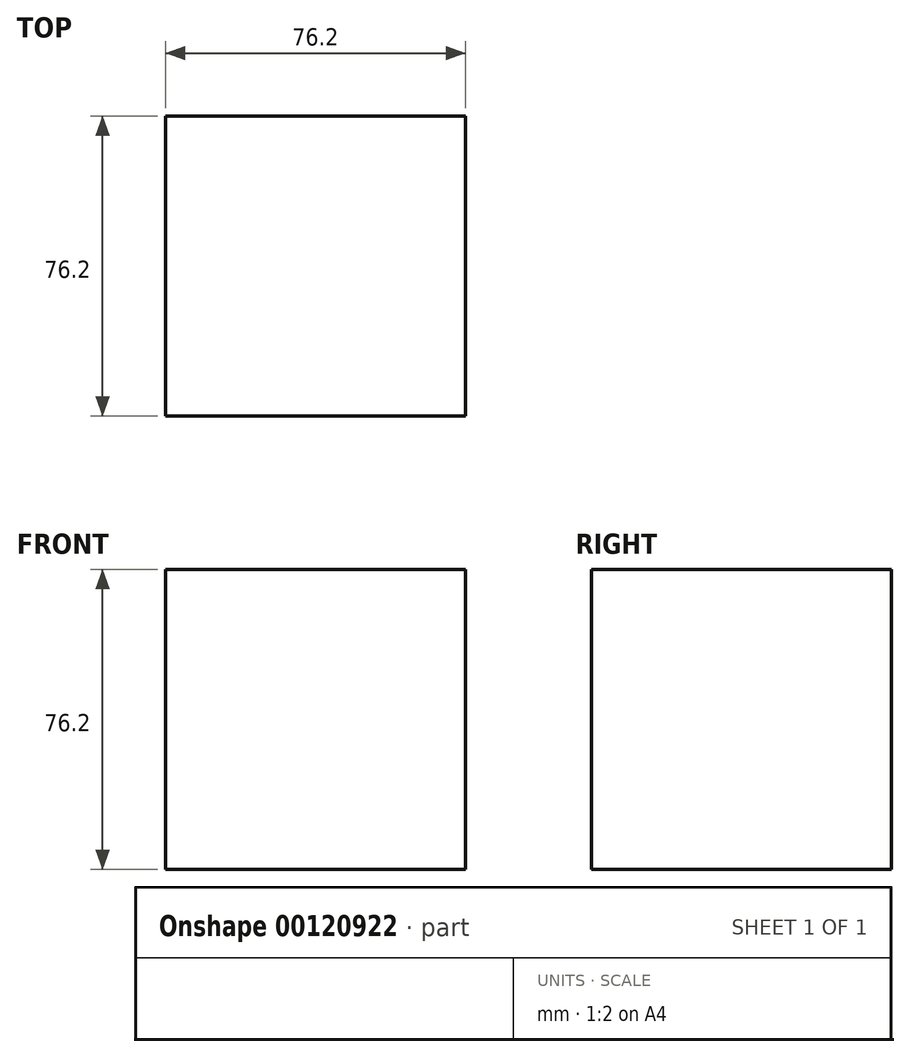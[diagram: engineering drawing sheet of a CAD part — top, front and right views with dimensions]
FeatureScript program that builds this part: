
annotation { "Feature Type Name" : "Feature", "Feature Type Description" : "" }
export const myFeature = defineFeature(function(context is Context, id is Id, definition is map)
    precondition{}
    {
        {
            var Q0;
            Q0=qCreatedBy(makeId("Top.planeOp"),FACE);
            var sketch = newSketch(context, id + "F0", { "sketchPlane" : qUnion([Q0])});
            skLineSegment(sketch, "E0.bottom", {"start": v(-45.4, 11.51) * mm, "end": v(30.8, 11.51) * mm});
            skLineSegment(sketch, "E0.top", {"start": v(-45.4, -64.69) * mm, "end": v(30.8, -64.69) * mm});
            skLineSegment(sketch, "E0.left", {"start": v(-45.4, 11.51) * mm, "end": v(-45.4, -64.69) * mm});
            skLineSegment(sketch, "E0.right", {"start": v(30.8, 11.51) * mm, "end": v(30.8, -64.69) * mm});
            skSolve(sketch);
        }
        {
            var Q0;
            Q0=makeQuery(id+"F0.imprint","IMPRINT",FACE,{"disambiguationData":[TD([[makeQuery(id+"F0.imprint","IMPRINT",EDGE,{"derivedFrom":sQuery(id+"F0.wireOp",EDGE,"E0.bottom")}),-1.0]])]});
            extrude(context, id + "F1", {"entities" : qUnion([Q0]), "depth" : 76.2 * mm});
        }
    });
